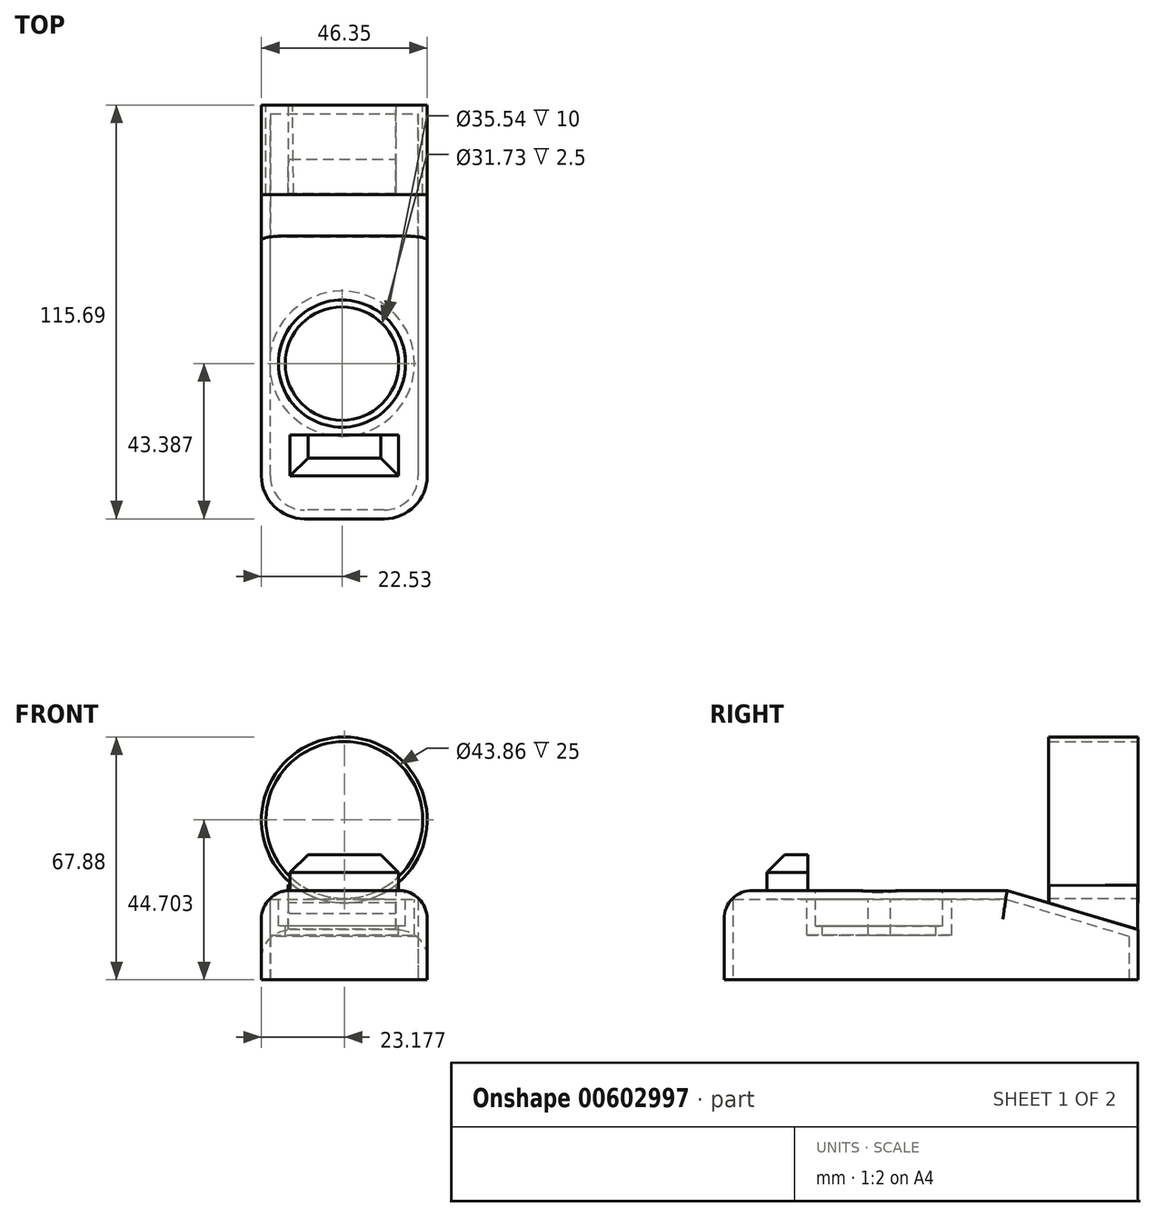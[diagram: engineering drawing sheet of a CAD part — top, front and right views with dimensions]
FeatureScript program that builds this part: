
annotation { "Feature Type Name" : "Feature", "Feature Type Description" : "" }
export const myFeature = defineFeature(function(context is Context, id is Id, definition is map)
    precondition{}
    {
        {
            var Q0;
            Q0=qCreatedBy(makeId("Top.planeOp"),FACE);
            var sketch = newSketch(context, id + "F0", { "sketchPlane" : qUnion([Q0])});
            skLineSegment(sketch, "E0", {"start": v(-15.36, 59.7) * mm, "end": v(30.99, 59.7) * mm});
            skLineSegment(sketch, "E1", {"start": v(30.99, 59.7) * mm, "end": v(30.99, -55.98) * mm});
            skLineSegment(sketch, "E2", {"start": v(30.99, -55.98) * mm, "end": v(-15.36, -55.98) * mm});
            skLineSegment(sketch, "E3", {"start": v(-15.36, -55.98) * mm, "end": v(-15.36, 59.7) * mm});
            skPoint(sketch, "E4.orphan", {"position": v(-21.91, 59.7) * mm});
            skSolve(sketch);
        }
        {
            var Q0;
            Q0=makeQuery(id+"F0.imprint","IMPRINT",FACE,{"disambiguationData":[TD([[makeQuery(id+"F0.imprint","IMPRINT",EDGE,{"derivedFrom":sQuery(id+"F0.wireOp",EDGE,"E0")}),-1.0]])]});
            extrude(context, id + "F1", {"entities" : qUnion([Q0]), "depth" : 25 * mm, "offsetDistance" : 25 * mm});
        }
        {
            var Q0;
            Q0=makeQuery(id+"F1.opExtrude","SWEPT_EDGE",EDGE,{"disambiguationData":[OSD([sQuery(id+"F0.wireOp",EDGE,"E1"),sQuery(id+"F0.wireOp",EDGE,"E2")])]});
            var Q1;
            Q1=makeQuery(id+"F1.opExtrude","SWEPT_EDGE",EDGE,{"disambiguationData":[OSD([sQuery(id+"F0.wireOp",EDGE,"E2"),sQuery(id+"F0.wireOp",EDGE,"E3")])]});
            fillet(context, id + "F2", {"entities" : qUnion([Q0, Q1]), "radius" : 12 * mm, "tangentPropagation" : true, "allowEdgeOverflow" : false});
        }
        {
            var Q0;
            Q0=qCreatedBy(makeId("Right.planeOp"),FACE);
            var sketch = newSketch(context, id + "F3", { "sketchPlane" : qUnion([Q0])});
            skLineSegment(sketch, "E5", {"start": v(68.29, 11.4) * mm, "end": v(0, 31.97) * mm});
            skLineSegment(sketch, "E6", {"start": v(0, 31.97) * mm, "end": v(67.64, 28.47) * mm});
            skLineSegment(sketch, "E7", {"start": v(67.64, 28.47) * mm, "end": v(68.29, 11.4) * mm});
            skSolve(sketch);
        }
        {
            var Q0;
            Q0 = qSketchRegion(id + "F3", true);
            extrude(context, id + "F4", {"entities" : qUnion([Q0]), "operationType" : NewBodyOperationType.REMOVE, "depth" : 40 * mm, "offsetDistance" : 25 * mm, "hasSecondDirection" : true, "secondDirectionOppositeDirection" : true, "secondDirectionDepth" : 40 * mm});
        }
        {
            var Q0;
            Q0=makeQuery(id+"F1.opExtrude","SWEPT_BODY",BODY,{"disambiguationData":[OSD([sQuery(id+"F0.wireOp",EDGE,"E0"),sQuery(id+"F0.wireOp",EDGE,"E1"),sQuery(id+"F0.wireOp",EDGE,"E2"),sQuery(id+"F0.wireOp",EDGE,"E3")])]});
            transform(context, id + "F5", {"entities" : qUnion([Q0]), "transformType" : TransformType.TRANSLATION_3D, "dx" : -7.17 * mm, "dy" : 0 * mm, "dz" : 0 * mm, "makeCopy" : false});
        }
        {
            var Q0;
            Q0=makeQuery(id+"F1.opExtrude","CAP_FACE",FACE,{"disambiguationData":[OSD([sQuery(id+"F0.wireOp",EDGE,"E0"),sQuery(id+"F0.wireOp",EDGE,"E1"),sQuery(id+"F0.wireOp",EDGE,"E2"),sQuery(id+"F0.wireOp",EDGE,"E3")])],"isStart":false});
            var sketch = newSketch(context, id + "F6", { "sketchPlane" : qUnion([Q0])});
            skCircle(sketch, "E8", {"center": v(0, -12.6) * mm, "radius": 17.77 * mm});
            skSolve(sketch);
        }
        {
            var Q0;
            Q0 = qSketchRegion(id + "F6", true);
            var Q1;
            Q1=makeQuery(id+"F6.imprint","IMPRINT",FACE,{"disambiguationData":[TD([[makeQuery(id+"F6.imprint","IMPRINT",EDGE,{"derivedFrom":sQuery(id+"F6.wireOp",EDGE,"E8")}),1.0]])]});
            extrude(context, id + "F7", {"entities" : qUnion([Q0, Q1]), "operationType" : NewBodyOperationType.REMOVE, "oppositeDirection" : true, "depth" : 10 * mm, "offsetDistance" : 25 * mm});
        }
        {
            var Q0;
            Q0=makeQuery(id+"F1.opExtrude","SWEPT_FACE",FACE,{"disambiguationData":[OSD([sQuery(id+"F0.wireOp",EDGE,"E0")])]});
            var sketch = newSketch(context, id + "F8", { "sketchPlane" : qUnion([Q0])});
            skCircle(sketch, "E9", {"center": v(-0.65, 33.93) * mm, "radius": 23.17 * mm});
            skPoint(sketch, "E9.centerSnap0", {"position": v(-0.65, 13.99) * mm});
            skSolve(sketch);
        }
        {
            var Q0;
            Q0 = qSketchRegion(id + "F8", true);
            extrude(context, id + "F9", {"entities" : qUnion([Q0]), "oppositeDirection" : true, "depth" : 25 * mm, "offsetDistance" : 25 * mm});
        }
        {
            var Q0;
            Q0=makeQuery(id+"F9.opExtrude","SWEPT_BODY",BODY,{"disambiguationData":[OSD([sQuery(id+"F8.wireOp",EDGE,"E9")])]});
            transform(context, id + "F10", {"entities" : qUnion([Q0]), "transformType" : TransformType.TRANSLATION_3D, "dx" : 0 * mm, "dy" : 0 * mm, "dz" : 10.78 * mm, "makeCopy" : false});
        }
        {
            var Q0;
            Q0=makeQuery(id+"F9.opExtrude","CAP_FACE",FACE,{"disambiguationData":[OSD([sQuery(id+"F8.wireOp",EDGE,"E9")])],"isStart":true});
            var sketch = newSketch(context, id + "F11", { "sketchPlane" : qUnion([Q0])});
            skCircle(sketch, "E10", {"center": v(-0.65, 44.7) * mm, "radius": 21.93 * mm});
            skSolve(sketch);
        }
        {
            var Q0;
            Q0 = qSketchRegion(id + "F11", true);
            extrude(context, id + "F12", {"entities" : qUnion([Q0]), "operationType" : NewBodyOperationType.REMOVE, "oppositeDirection" : true, "depth" : 25 * mm, "offsetDistance" : 25 * mm});
        }
        {
            var Q0;
            Q0=qCreatedBy(makeId("Right.planeOp"),FACE);
            var sketch = newSketch(context, id + "F13", { "sketchPlane" : qUnion([Q0])});
            skLineSegment(sketch, "E11", {"start": v(59.62, 21.59) * mm, "end": v(59.62, 14.13) * mm});
            skLineSegment(sketch, "E12", {"start": v(59.62, 14.13) * mm, "end": v(34.92, 21.38) * mm});
            skLineSegment(sketch, "E13", {"start": v(59.62, 21.59) * mm, "end": v(34.92, 21.38) * mm});
            skSolve(sketch);
        }
        {
            var Q0;
            Q0 = qSketchRegion(id + "F13", true);
            extrude(context, id + "F14", {"entities" : qUnion([Q0]), "depth" : 15 * mm, "offsetDistance" : 25 * mm, "hasSecondDirection" : true, "secondDirectionOppositeDirection" : true, "secondDirectionDepth" : 15 * mm});
        }
        {
            var Q0;
            Q0=makeQuery(id+"F1.opExtrude","CAP_FACE",FACE,{"disambiguationData":[OSD([sQuery(id+"F0.wireOp",EDGE,"E0"),sQuery(id+"F0.wireOp",EDGE,"E1"),sQuery(id+"F0.wireOp",EDGE,"E2"),sQuery(id+"F0.wireOp",EDGE,"E3")])],"isStart":true});
            shell(context, id + "F15", {"entities" : qUnion([Q0]), "thickness" : 2.5 * mm});
        }
        {
            var Q0;
            Q0=makeQuery(id+"F7.boolean.opBoolean","COPY",FACE,{"derivedFrom":makeQuery(id+"F7.opExtrude","CAP_FACE",FACE,{"disambiguationData":[OSD([sQuery(id+"F6.wireOp",EDGE,"E8")])],"isStart":false})});
            var sketch = newSketch(context, id + "F16", { "sketchPlane" : qUnion([Q0])});
            skCircle(sketch, "E14", {"center": v(0, -12.6) * mm, "radius": 15.86 * mm});
            skSolve(sketch);
        }
        {
            var Q0;
            Q0 = qSketchRegion(id + "F16", true);
            extrude(context, id + "F17", {"entities" : qUnion([Q0]), "operationType" : NewBodyOperationType.REMOVE, "oppositeDirection" : true, "depth" : 25 * mm, "offsetDistance" : 25 * mm});
        }
        {
            var Q0;
            Q0=makeQuery(id+"F14.opExtrude","SWEPT_FACE",FACE,{"disambiguationData":[OSD([sQuery(id+"F13.wireOp",EDGE,"E13")])]});
            extrude(context, id + "F18", {"entities" : qUnion([Q0]), "operationType" : NewBodyOperationType.ADD, "depth" : 5 * mm, "offsetDistance" : 25 * mm});
        }
        {
            var Q0;
            Q0=makeQuery(id+"F11.imprint","IMPRINT",FACE,{"disambiguationData":[TD([[makeQuery(id+"F11.imprint","IMPRINT",EDGE,{"derivedFrom":sQuery(id+"F11.wireOp",EDGE,"E10")}),1.0]])]});
            extrude(context, id + "F19", {"entities" : qUnion([Q0]), "operationType" : NewBodyOperationType.REMOVE, "oppositeDirection" : true, "depth" : 25 * mm, "offsetDistance" : 25 * mm});
        }
        {
            var Q0;
            Q0=makeQuery(id+"F1.opExtrude","CAP_EDGE",EDGE,{"disambiguationData":[OSD([sQuery(id+"F0.wireOp",EDGE,"E1")])],"isStart":false});
            var Q1;
            {var subQ0=sQuery(id+"F0.wireOp",EDGE,"E2");var subQ1=sQuery(id+"F0.wireOp",EDGE,"E1");Q1=makeQuery(id+"F2.opFillet","BLEND_EDGE",EDGE,{"blendedFrom":[makeQuery(id+"F1.opExtrude","SWEPT_EDGE",EDGE,{"disambiguationData":[OSD([subQ1,subQ0])]}),makeQuery(id+"F1.opExtrude","CAP_FACE",FACE,{"disambiguationData":[OSD([sQuery(id+"F0.wireOp",EDGE,"E0"),subQ1,subQ0,sQuery(id+"F0.wireOp",EDGE,"E3")])],"isStart":false})],"blendedInto":[makeQuery(id+"F1.opExtrude","CAP_FACE",FACE,{"disambiguationData":[OSD([sQuery(id+"F0.wireOp",EDGE,"E0"),subQ1,subQ0,sQuery(id+"F0.wireOp",EDGE,"E3")])],"isStart":false})]});}
            var Q2;
            Q2=makeQuery(id+"F4.boolean.opBoolean","INTERSECT",EDGE,{"derivedFrom":[makeQuery(id+"F1.opExtrude","SWEPT_FACE",FACE,{"disambiguationData":[OSD([sQuery(id+"F0.wireOp",EDGE,"E1")])]}),makeQuery(id+"F4.opExtrude","SWEPT_FACE",FACE,{"disambiguationData":[OSD([sQuery(id+"F3.wireOp",EDGE,"E5")])]})]});
            var Q3;
            Q3=makeQuery(id+"F4.boolean.opBoolean","INTERSECT",EDGE,{"derivedFrom":[makeQuery(id+"F1.opExtrude","SWEPT_FACE",FACE,{"disambiguationData":[OSD([sQuery(id+"F0.wireOp",EDGE,"E3")])]}),makeQuery(id+"F4.opExtrude","SWEPT_FACE",FACE,{"disambiguationData":[OSD([sQuery(id+"F3.wireOp",EDGE,"E5")])]})]});
            fillet(context, id + "F20", {"entities" : qUnion([Q0, Q1, Q2, Q3]), "radius" : 8 * mm, "tangentPropagation" : true, "allowEdgeOverflow" : false});
        }
        {
            var Q0;
            Q0=makeQuery(id+"F20.opFillet","SPLIT",FACE,{"disambiguationData":[OD(0.0)],"derivedFrom":makeQuery(id+"F1.opExtrude","CAP_FACE",FACE,{"disambiguationData":[OSD([sQuery(id+"F0.wireOp",EDGE,"E0"),sQuery(id+"F0.wireOp",EDGE,"E1"),sQuery(id+"F0.wireOp",EDGE,"E2"),sQuery(id+"F0.wireOp",EDGE,"E3")])],"isStart":false})});
            var sketch = newSketch(context, id + "F21", { "sketchPlane" : qUnion([Q0])});
            skLineSegment(sketch, "E15.bottom", {"start": v(-14.53, -32.54) * mm, "end": v(15.82, -32.54) * mm});
            skLineSegment(sketch, "E15.top", {"start": v(-14.53, -43.98) * mm, "end": v(15.82, -43.98) * mm});
            skLineSegment(sketch, "E15.left", {"start": v(-14.53, -32.54) * mm, "end": v(-14.53, -43.98) * mm});
            skLineSegment(sketch, "E15.right", {"start": v(15.82, -32.54) * mm, "end": v(15.82, -43.98) * mm});
            skSolve(sketch);
        }
        {
            var Q0;
            Q0=makeQuery(id+"F21.imprint","IMPRINT",FACE,{"disambiguationData":[TD([[makeQuery(id+"F21.imprint","IMPRINT",EDGE,{"derivedFrom":sQuery(id+"F21.wireOp",EDGE,"E15.bottom")}),-1.0]])]});
            extrude(context, id + "F22", {"entities" : qUnion([Q0]), "operationType" : NewBodyOperationType.ADD, "depth" : 10 * mm, "offsetDistance" : 25 * mm});
        }
        {
            var Q0;
            Q0=makeQuery(id+"F22.opExtrude","CAP_EDGE",EDGE,{"disambiguationData":[OSD([sQuery(id+"F21.wireOp",EDGE,"E15.right")])],"isStart":false});
            var Q1;
            Q1=makeQuery(id+"F22.opExtrude","CAP_EDGE",EDGE,{"disambiguationData":[OSD([sQuery(id+"F21.wireOp",EDGE,"E15.left")])],"isStart":false});
            var Q2;
            Q2=makeQuery(id+"F22.opExtrude","CAP_EDGE",EDGE,{"disambiguationData":[OSD([sQuery(id+"F21.wireOp",EDGE,"E15.top")])],"isStart":false});
            chamfer(context, id + "F23", {"entities" : qUnion([Q0, Q1, Q2]), "width" : 5 * mm, "tangentPropagation" : true});
        }
    });
